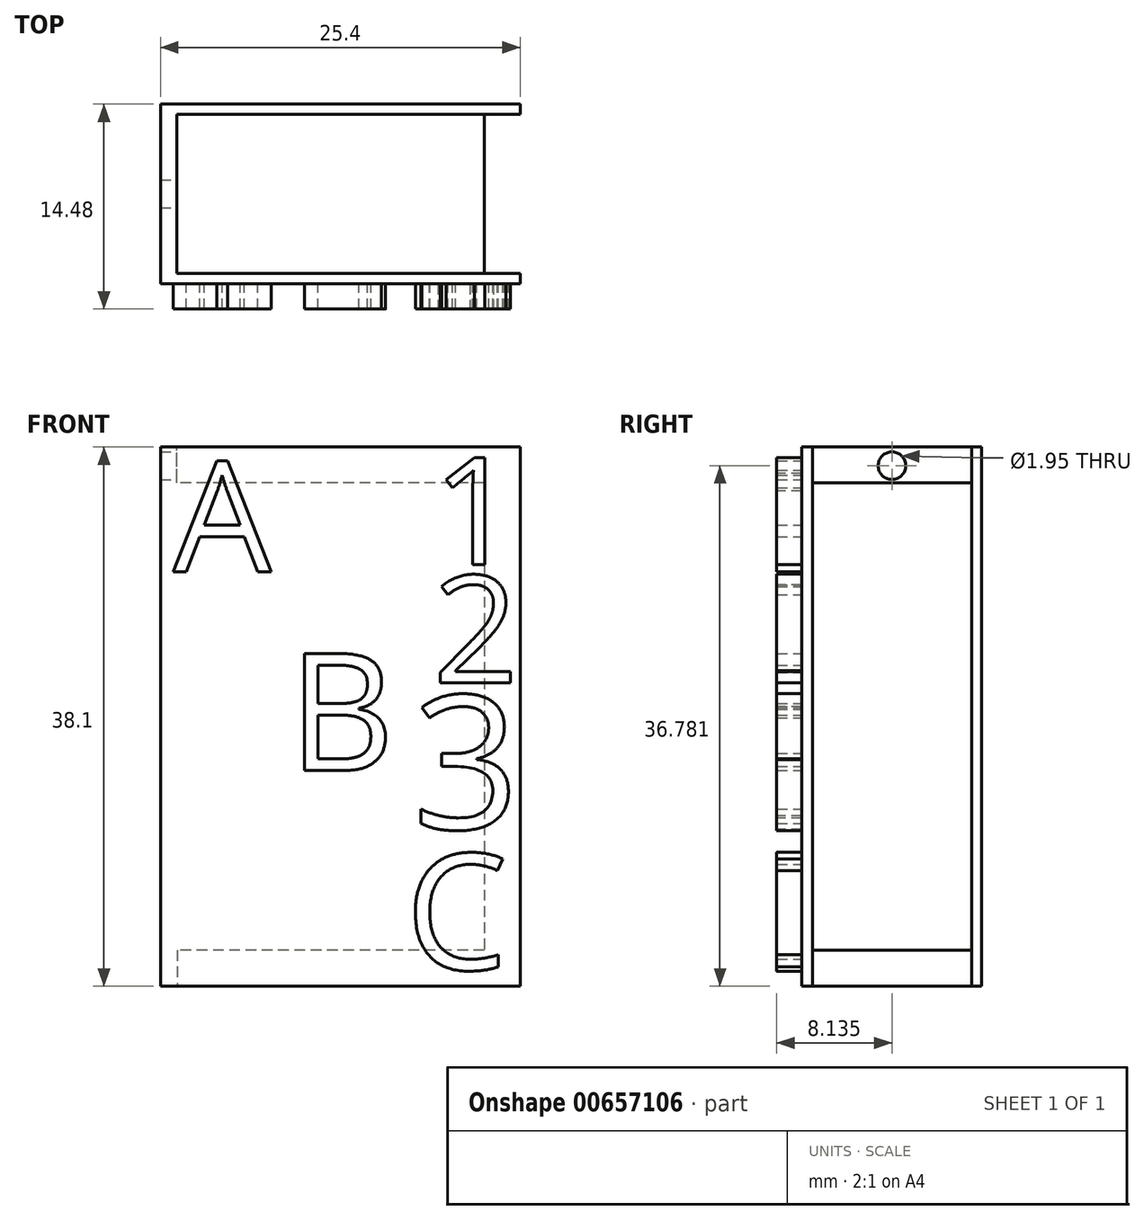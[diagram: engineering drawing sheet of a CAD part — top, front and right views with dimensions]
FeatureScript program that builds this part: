
annotation { "Feature Type Name" : "Feature", "Feature Type Description" : "" }
export const myFeature = defineFeature(function(context is Context, id is Id, definition is map)
    precondition{}
    {
        {
            var Q0;
            Q0=qCreatedBy(makeId("Front.planeOp"),FACE);
            var sketch = newSketch(context, id + "F0", { "sketchPlane" : qUnion([Q0])});
            skLineSegment(sketch, "E0.bottom", {"start": v(-25.4, 32.44) * mm, "end": v(0, 32.44) * mm});
            skLineSegment(sketch, "E0.top", {"start": v(-25.4, -5.66) * mm, "end": v(0, -5.66) * mm});
            skLineSegment(sketch, "E0.left", {"start": v(-25.4, 32.44) * mm, "end": v(-25.4, -5.66) * mm});
            skLineSegment(sketch, "E0.right", {"start": v(0, 32.44) * mm, "end": v(0, -5.66) * mm});
            skSolve(sketch);
        }
        {
            var Q0;
            Q0 = qSketchRegion(id + "F0", true);
            extrude(context, id + "F1", {"entities" : qUnion([Q0]), "depth" : 12.7 * mm, "offsetDistance" : 25.4 * mm});
        }
        {
            var Q0;
            Q0=makeQuery(id+"F1.opExtrude","SWEPT_FACE",FACE,{"disambiguationData":[OSD([sQuery(id+"F0.wireOp",EDGE,"E0.right")])]});
            var sketch = newSketch(context, id + "F2", { "sketchPlane" : qUnion([Q0])});
            skLineSegment(sketch, "E1", {"start": v(-0.73, -5.66) * mm, "end": v(-0.73, 32.44) * mm});
            skLineSegment(sketch, "E2", {"start": v(-11.96, 32.44) * mm, "end": v(-11.96, -5.66) * mm});
            skSolve(sketch);
        }
        {
            var Q0;
            {var subQ0=sQuery(id+"F2.wireOp",EDGE,"E1");Q0=makeQuery(id+"F2.imprint","IMPRINT",FACE,{"disambiguationData":[TD([[makeQuery(id+"F2.imprint","IMPRINT",EDGE,{"derivedFrom":subQ0}),1.0]])]});}
            extrude(context, id + "F3", {"entities" : qUnion([Q0]), "operationType" : NewBodyOperationType.REMOVE, "oppositeDirection" : true, "depth" : 2.54 * mm, "offsetDistance" : 25.4 * mm});
        }
        {
            var Q0;
            Q0=makeQuery(id+"F1.opExtrude","SWEPT_FACE",FACE,{"disambiguationData":[OSD([sQuery(id+"F0.wireOp",EDGE,"E0.bottom")])]});
            var sketch = newSketch(context, id + "F4", { "sketchPlane" : qUnion([Q0])});
            skLineSegment(sketch, "E3", {"start": v(-2.54, -11.96) * mm, "end": v(-24.24, -11.96) * mm});
            skLineSegment(sketch, "E4", {"start": v(-2.54, -0.73) * mm, "end": v(-24.24, -0.73) * mm});
            skLineSegment(sketch, "E5", {"start": v(-24.24, -11.96) * mm, "end": v(-24.24, -0.73) * mm});
            skSolve(sketch);
        }
        {
            var Q0;
            Q0=makeQuery(id+"F4.imprint","IMPRINT",FACE,{"disambiguationData":[TD([[makeQuery(id+"F4.imprint","IMPRINT",EDGE,{"derivedFrom":sQuery(id+"F4.wireOp",EDGE,"E3")}),-1.0]])]});
            extrude(context, id + "F5", {"entities" : qUnion([Q0]), "operationType" : NewBodyOperationType.REMOVE, "oppositeDirection" : true, "depth" : 2.54 * mm, "offsetDistance" : 25.4 * mm});
        }
        {
            var Q0;
            Q0=makeQuery(id+"F1.opExtrude","SWEPT_FACE",FACE,{"disambiguationData":[OSD([sQuery(id+"F0.wireOp",EDGE,"E0.top")])]});
            var sketch = newSketch(context, id + "F6", { "sketchPlane" : qUnion([Q0])});
            skLineSegment(sketch, "E6", {"start": v(-2.54, 0.73) * mm, "end": v(-24.23, 0.73) * mm});
            skLineSegment(sketch, "E7", {"start": v(-2.54, 11.96) * mm, "end": v(-24.23, 11.96) * mm});
            skLineSegment(sketch, "E8", {"start": v(-24.23, 0.73) * mm, "end": v(-24.23, 11.96) * mm});
            skSolve(sketch);
        }
        {
            var Q0;
            Q0=makeQuery(id+"F6.imprint","IMPRINT",FACE,{"disambiguationData":[TD([[makeQuery(id+"F6.imprint","IMPRINT",EDGE,{"derivedFrom":sQuery(id+"F6.wireOp",EDGE,"E6")}),-1.0]])]});
            extrude(context, id + "F7", {"entities" : qUnion([Q0]), "operationType" : NewBodyOperationType.REMOVE, "oppositeDirection" : true, "depth" : 2.54 * mm, "offsetDistance" : 25.4 * mm});
        }
        {
            var Q0;
            Q0=makeQuery(id+"F3.boolean.opBoolean","COPY",FACE,{"derivedFrom":makeQuery(id+"F3.opExtrude","CAP_FACE",FACE,{"disambiguationData":[OSD([sQuery(id+"F0.wireOp",EDGE,"E0.bottom"),sQuery(id+"F0.wireOp",EDGE,"E0.top"),sQuery(id+"F0.wireOp",EDGE,"E0.right"),sQuery(id+"F2.wireOp",EDGE,"E1"),sQuery(id+"F2.wireOp",EDGE,"E2")])],"isStart":false})});
            var sketch = newSketch(context, id + "F8", { "sketchPlane" : qUnion([Q0])});
            skLineSegment(sketch, "E9.bottom", {"start": v(-11.42, 29.9) * mm, "end": v(-10.92, 29.9) * mm});
            skLineSegment(sketch, "E9.top", {"start": v(-11.42, -3.12) * mm, "end": v(-10.92, -3.12) * mm});
            skLineSegment(sketch, "E9.left", {"start": v(-11.42, 29.9) * mm, "end": v(-11.42, -3.12) * mm});
            skLineSegment(sketch, "E9.right", {"start": v(-10.92, 29.9) * mm, "end": v(-10.92, -3.12) * mm});
            skLineSegment(sketch, "E10.bottom", {"start": v(-10.13, 29.9) * mm, "end": v(-9.56, 29.9) * mm});
            skLineSegment(sketch, "E10.top", {"start": v(-10.13, -3.12) * mm, "end": v(-9.56, -3.12) * mm});
            skLineSegment(sketch, "E10.left", {"start": v(-10.13, 29.9) * mm, "end": v(-10.13, -3.12) * mm});
            skLineSegment(sketch, "E10.right", {"start": v(-9.56, 29.9) * mm, "end": v(-9.56, -3.12) * mm});
            skLineSegment(sketch, "E11.bottom", {"start": v(-8.78, 29.9) * mm, "end": v(-8.21, 29.9) * mm});
            skLineSegment(sketch, "E11.top", {"start": v(-8.78, -3.12) * mm, "end": v(-8.21, -3.12) * mm});
            skLineSegment(sketch, "E11.left", {"start": v(-8.78, 29.9) * mm, "end": v(-8.78, -3.12) * mm});
            skLineSegment(sketch, "E11.right", {"start": v(-8.21, 29.9) * mm, "end": v(-8.21, -3.12) * mm});
            skLineSegment(sketch, "E12.bottom", {"start": v(-7.56, 29.9) * mm, "end": v(-7, 29.9) * mm});
            skLineSegment(sketch, "E12.top", {"start": v(-7.56, -3.12) * mm, "end": v(-7, -3.12) * mm});
            skLineSegment(sketch, "E12.left", {"start": v(-7.56, 29.9) * mm, "end": v(-7.56, -3.12) * mm});
            skLineSegment(sketch, "E12.right", {"start": v(-7, 29.9) * mm, "end": v(-7, -3.12) * mm});
            skLineSegment(sketch, "E13.bottom", {"start": v(-6.35, 29.9) * mm, "end": v(-5.78, 29.9) * mm});
            skLineSegment(sketch, "E13.top", {"start": v(-6.35, -3.12) * mm, "end": v(-5.78, -3.12) * mm});
            skLineSegment(sketch, "E13.left", {"start": v(-6.35, 29.9) * mm, "end": v(-6.35, -3.12) * mm});
            skLineSegment(sketch, "E13.right", {"start": v(-5.78, 29.9) * mm, "end": v(-5.78, -3.12) * mm});
            skLineSegment(sketch, "E14.bottom", {"start": v(-5.06, 29.9) * mm, "end": v(-4.49, 29.9) * mm});
            skLineSegment(sketch, "E14.top", {"start": v(-5.06, -3.12) * mm, "end": v(-4.49, -3.12) * mm});
            skLineSegment(sketch, "E14.left", {"start": v(-5.06, 29.9) * mm, "end": v(-5.06, -3.12) * mm});
            skLineSegment(sketch, "E14.right", {"start": v(-4.49, 29.9) * mm, "end": v(-4.49, -3.12) * mm});
            skLineSegment(sketch, "E15.bottom", {"start": v(-3.84, 29.9) * mm, "end": v(-3.28, 29.9) * mm});
            skLineSegment(sketch, "E15.top", {"start": v(-3.84, -3.12) * mm, "end": v(-3.28, -3.12) * mm});
            skLineSegment(sketch, "E15.left", {"start": v(-3.84, 29.9) * mm, "end": v(-3.84, -3.12) * mm});
            skLineSegment(sketch, "E15.right", {"start": v(-3.28, 29.9) * mm, "end": v(-3.28, -3.12) * mm});
            skLineSegment(sketch, "E16.bottom", {"start": v(-2.55, 29.9) * mm, "end": v(-1.98, 29.9) * mm});
            skLineSegment(sketch, "E16.top", {"start": v(-2.55, -3.12) * mm, "end": v(-1.98, -3.12) * mm});
            skLineSegment(sketch, "E16.left", {"start": v(-2.55, 29.9) * mm, "end": v(-2.55, -3.12) * mm});
            skLineSegment(sketch, "E16.right", {"start": v(-1.98, 29.9) * mm, "end": v(-1.98, -3.12) * mm});
            skSolve(sketch);
        }
        {
            var Q0;
            Q0=sQuery(id+"F8.wireOp",EDGE,"E9.left");
            var Q1;
            Q1=sQuery(id+"F8.wireOp",EDGE,"E9.right");
            var Q2;
            Q2=sQuery(id+"F8.wireOp",EDGE,"E10.left");
            var Q3;
            Q3=sQuery(id+"F8.wireOp",EDGE,"E10.right");
            var Q4;
            Q4=sQuery(id+"F8.wireOp",EDGE,"E11.left");
            var Q5;
            Q5=sQuery(id+"F8.wireOp",EDGE,"E11.right");
            var Q6;
            Q6=sQuery(id+"F8.wireOp",EDGE,"E12.left");
            var Q7;
            Q7=sQuery(id+"F8.wireOp",EDGE,"E12.right");
            var Q8;
            Q8=sQuery(id+"F8.wireOp",EDGE,"E13.right");
            var Q9;
            Q9=sQuery(id+"F8.wireOp",EDGE,"E13.left");
            var Q10;
            Q10=sQuery(id+"F8.wireOp",EDGE,"E14.left");
            var Q11;
            Q11=sQuery(id+"F8.wireOp",EDGE,"E14.right");
            var Q12;
            Q12=sQuery(id+"F8.wireOp",EDGE,"E15.left");
            var Q13;
            Q13=sQuery(id+"F8.wireOp",EDGE,"E15.right");
            var Q14;
            Q14=sQuery(id+"F8.wireOp",EDGE,"E16.left");
            var Q15;
            Q15=sQuery(id+"F8.wireOp",EDGE,"E16.right");
            extrude(context, id + "F9", {"bodyType" : ToolBodyType.SURFACE, "surfaceEntities" : qUnion([Q0, Q1, Q2, Q3, Q4, Q5, Q6, Q7, Q8, Q9, Q10, Q11, Q12, Q13, Q14, Q15]), "oppositeDirection" : true, "depth" : 20.32 * mm, "offsetDistance" : 25.4 * mm});
        }
        {
            var Q0;
            Q0=makeQuery(id+"F5.boolean.opBoolean","COPY",FACE,{"derivedFrom":makeQuery(id+"F5.opExtrude","SWEPT_FACE",FACE,{"disambiguationData":[OSD([sQuery(id+"F4.wireOp",EDGE,"E5")])]})});
            var sketch = newSketch(context, id + "F10", { "sketchPlane" : qUnion([Q0])});
            skCircle(sketch, "E17", {"center": v(-6.35, 31.12) * mm, "radius": 0.98 * mm});
            skPoint(sketch, "E17.centerSnap0", {"position": v(-6.35, 29.9) * mm});
            skSolve(sketch);
        }
        {
            var Q0;
            Q0 = qSketchRegion(id + "F10", true);
            extrude(context, id + "F11", {"entities" : qUnion([Q0]), "operationType" : NewBodyOperationType.REMOVE, "oppositeDirection" : true, "depth" : 25.4 * mm, "offsetDistance" : 25.4 * mm});
        }
        {
            var Q0;
            Q0=makeQuery(id+"F1.opExtrude","CAP_FACE",FACE,{"disambiguationData":[OSD([sQuery(id+"F0.wireOp",EDGE,"E0.bottom"),sQuery(id+"F0.wireOp",EDGE,"E0.top"),sQuery(id+"F0.wireOp",EDGE,"E0.left"),sQuery(id+"F0.wireOp",EDGE,"E0.right")])],"isStart":false});
            var sketch = newSketch(context, id + "F12", { "sketchPlane" : qUnion([Q0])});
            skText(sketch, "E18", { "text": "A ", "fontName": "OpenSans-Regular.ttf"});
            skText(sketch, "E19", { "text": "B", "fontName": "OpenSans-Regular.ttf"});
            skText(sketch, "E20", { "text": "C", "fontName": "OpenSans-Regular.ttf"});
            skText(sketch, "E21", { "text": "1", "fontName": "OpenSans-Regular.ttf"});
            skText(sketch, "E22", { "text": "2", "fontName": "OpenSans-Regular.ttf"});
            skText(sketch, "E23", { "text": "3", "fontName": "OpenSans-Regular.ttf"});
            const initialGuessF12  = {"E18": [-0.0245, 0.02363, 1, 0, 0.00786], "E19": [-0.01638, 0.00959, 1, 0, 0.00834], "E20": [-0.0081, -0.00448, 1, 0, 0.00824], "E21": [-0.0062, 0.02414, 1, 0, 0.00762], "E22": [-0.00617, 0.01579, 1, 0, 0.00762], "E23": [-0.0076, 0.00546, 1, 0, 0.0095]};
            skSetInitialGuess(sketch, initialGuessF12);
            skSolve(sketch);
        }
        {
            var Q0;
            Q0 = qSketchRegion(id + "F12", true);
            extrude(context, id + "F13", {"entities" : qUnion([Q0]), "operationType" : NewBodyOperationType.ADD, "depth" : 1.78 * mm, "offsetDistance" : 25.4 * mm});
        }
    });
